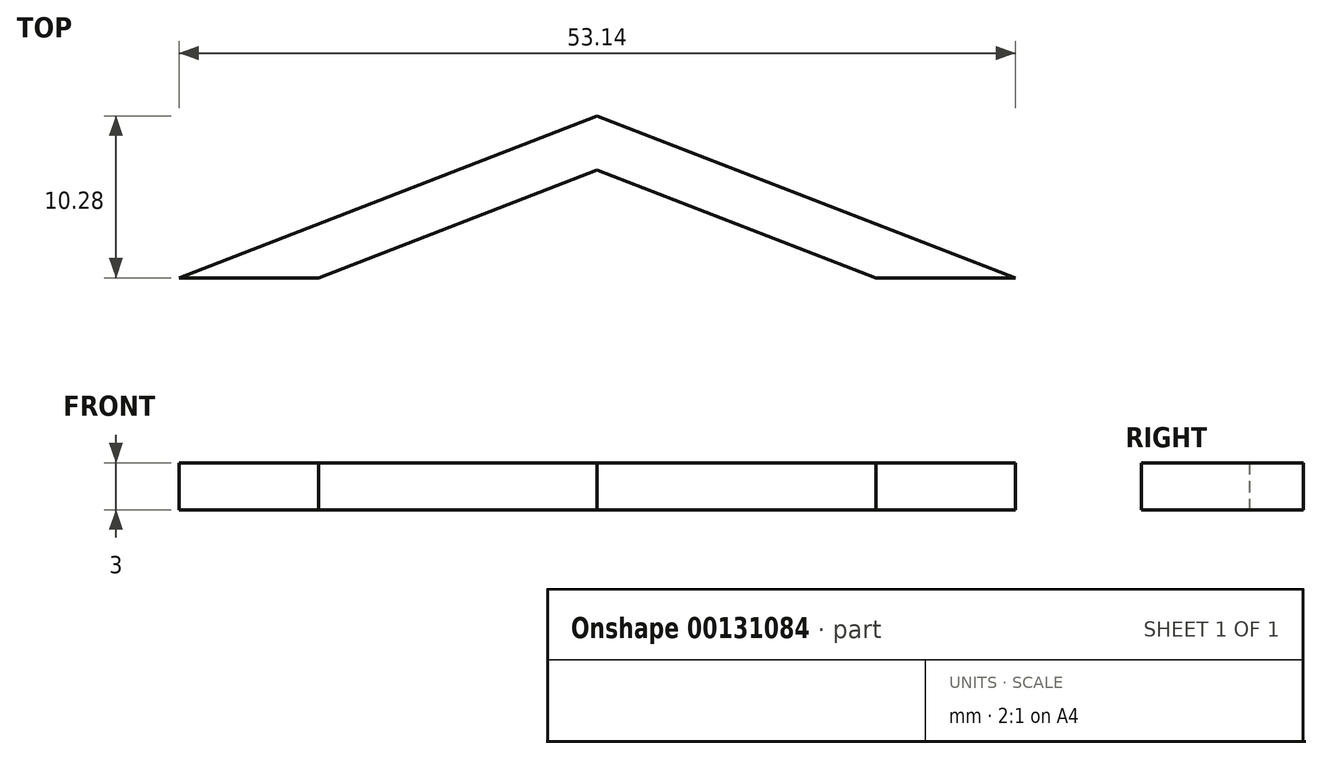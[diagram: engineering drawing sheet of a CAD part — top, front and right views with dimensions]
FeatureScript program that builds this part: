
annotation { "Feature Type Name" : "Feature", "Feature Type Description" : "" }
export const myFeature = defineFeature(function(context is Context, id is Id, definition is map)
    precondition{}
    {
        {
            var Q0;
            Q0=qCreatedBy(makeId("Top.planeOp"),FACE);
            var sketch = newSketch(context, id + "F0", { "sketchPlane" : qUnion([Q0])});
            skLineSegment(sketch, "E0", {"start": v(0, 37.5) * mm, "end": v(0, 49.5) * mm, "construction": true});
            skLineSegment(sketch, "E1", {"start": v(0, 43.5) * mm, "end": v(34.2, 43.5) * mm, "construction": true});
            skLineSegment(sketch, "E2", {"start": v(0, 43.5) * mm, "end": v(-40.16, 43.5) * mm, "construction": true});
            skLineSegment(sketch, "E3", {"start": v(34.2, 37.5) * mm, "end": v(34.2, 43.5) * mm, "construction": true});
            skLineSegment(sketch, "E4", {"start": v(-26.57, 39.22) * mm, "end": v(0, 49.5) * mm});
            skLineSegment(sketch, "E5", {"start": v(0, 49.5) * mm, "end": v(26.57, 39.22) * mm});
            skLineSegment(sketch, "E6", {"start": v(0, 49.5) * mm, "end": v(0, 46.3) * mm, "construction": true});
            skLineSegment(sketch, "E7", {"start": v(0, 46.07) * mm, "end": v(-17.7, 39.22) * mm, "construction": true});
            skLineSegment(sketch, "E8.MirrorCS", {"start": v(0, 46.07) * mm, "end": v(17.7, 39.22) * mm, "construction": true});
            skLineSegment(sketch, "E9", {"start": v(0, 46.07) * mm, "end": v(17.7, 39.22) * mm});
            skLineSegment(sketch, "E10", {"start": v(0, 46.07) * mm, "end": v(-17.7, 39.22) * mm});
            skLineSegment(sketch, "E11", {"start": v(-26.57, 39.22) * mm, "end": v(-17.7, 39.22) * mm});
            skPoint(sketch, "E11.startSnap0", {"position": v(-26.57, 37.5) * mm});
            skLineSegment(sketch, "E12.MirrorCS", {"start": v(26.57, 39.22) * mm, "end": v(17.7, 39.22) * mm});
            skPoint(sketch, "E13.orphan", {"position": v(-22.14, 37.5) * mm});
            skPoint(sketch, "E14.start.orphan", {"position": v(-31, 37.5) * mm});
            skPoint(sketch, "E15.start.orphan", {"position": v(22.14, 37.5) * mm});
            skPoint(sketch, "E16.orphan", {"position": v(31, 37.5) * mm});
            skSolve(sketch);
        }
        {
            var Q0;
            Q0=qSketchRegion(id+"F0",true);
            extrude(context, id + "F1", {"entities" : qUnion([Q0]), "endBound" : BoundingType.SYMMETRIC, "depth" : 3 * mm});
        }
    });
